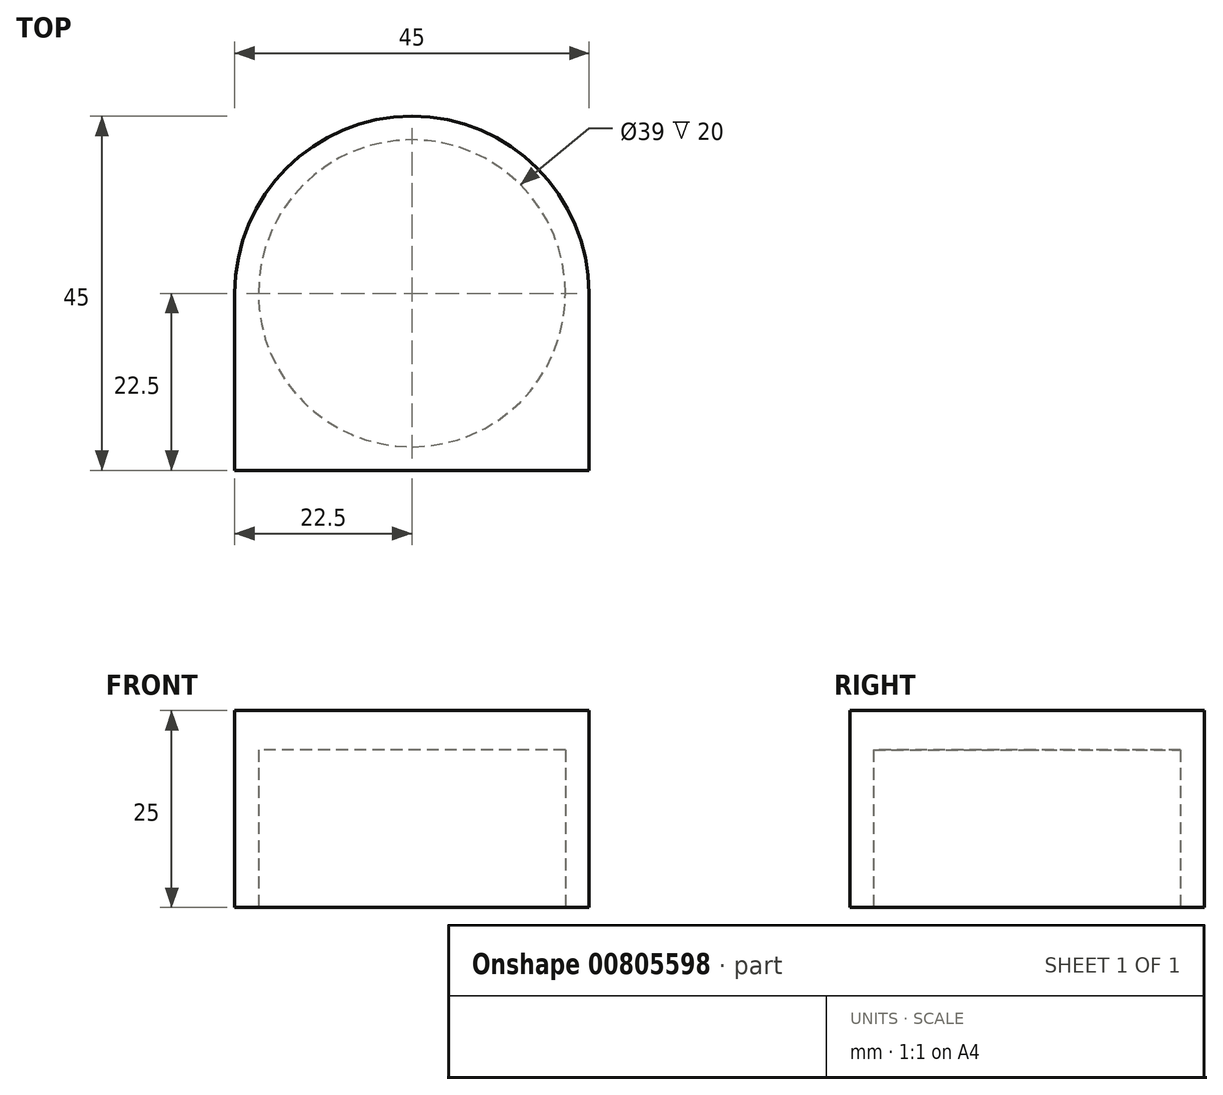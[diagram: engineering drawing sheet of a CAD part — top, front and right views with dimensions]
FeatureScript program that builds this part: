
annotation { "Feature Type Name" : "Feature", "Feature Type Description" : "" }
export const myFeature = defineFeature(function(context is Context, id is Id, definition is map)
    precondition{}
    {
        {
            var Q0;
            Q0=qCreatedBy(makeId("Top.planeOp"),FACE);
            var sketch = newSketch(context, id + "F0", { "sketchPlane" : qUnion([Q0])});
            skCircle(sketch, "E0", {"center": v(0, 0) * mm, "radius": 22.5 * mm});
            skSolve(sketch);
        }
        {
            var Q0;
            Q0 = qSketchRegion(id + "F0", true);
            extrude(context, id + "F1", {"entities" : qUnion([Q0]), "depth" : 25 * mm, "offsetDistance" : 25 * mm});
        }
        {
            var Q0;
            Q0=qCreatedBy(makeId("Top.planeOp"),FACE);
            var sketch = newSketch(context, id + "F2", { "sketchPlane" : qUnion([Q0])});
            skCircle(sketch, "E1", {"center": v(0, 0) * mm, "radius": 19.5 * mm});
            skSolve(sketch);
        }
        {
            var Q0;
            Q0 = qSketchRegion(id + "F2", true);
            extrude(context, id + "F3", {"entities" : qUnion([Q0]), "operationType" : NewBodyOperationType.REMOVE, "depth" : 20 * mm, "offsetDistance" : 25 * mm});
        }
        {
            var Q0;
            Q0=makeQuery(id+"F1.opExtrude","CAP_FACE",FACE,{"disambiguationData":[OSD([sQuery(id+"F0.wireOp",EDGE,"E0")])],"isStart":true});
            var sketch = newSketch(context, id + "F4", { "sketchPlane" : qUnion([Q0])});
            skLineSegment(sketch, "E2.bottom", {"start": v(22.5, -22.5) * mm, "end": v(-22.5, -22.5) * mm});
            skLineSegment(sketch, "E2.top", {"start": v(22.5, 22.5) * mm, "end": v(-22.5, 22.5) * mm});
            skLineSegment(sketch, "E2.left", {"start": v(22.5, -22.5) * mm, "end": v(22.5, 22.5) * mm});
            skLineSegment(sketch, "E2.right", {"start": v(-22.5, -22.5) * mm, "end": v(-22.5, 22.5) * mm});
            skPoint(sketch, "E2.middle", {"position": v(0, 0) * mm});
            skSolve(sketch);
        }
        {
            var Q0;
            {var subQ0=sQuery(id+"F4.wireOp",EDGE,"E2.right");var subQ1=sQuery(id+"F4.wireOp",EDGE,"E2.top");var subQ2=makeQuery(id+"F4.imprint","INTERSECT",VERTEX,{"derivedFrom":[subQ1,subQ0]});Q0=makeQuery(id+"F4.imprint","IMPRINT",FACE,{"disambiguationData":[TD([[makeQuery(id+"F4.imprint","IMPRINT",EDGE,{"disambiguationData":[TD([[subQ2,1.0]])],"derivedFrom":subQ1}),1.0]])]});}
            var Q1;
            {var subQ0=sQuery(id+"F4.wireOp",EDGE,"E2.left");var subQ1=sQuery(id+"F4.wireOp",EDGE,"E2.top");var subQ2=makeQuery(id+"F4.imprint","INTERSECT",VERTEX,{"derivedFrom":[subQ1,subQ0]});Q1=makeQuery(id+"F4.imprint","IMPRINT",FACE,{"disambiguationData":[TD([[makeQuery(id+"F4.imprint","IMPRINT",EDGE,{"disambiguationData":[TD([[subQ2,-1.0]])],"derivedFrom":subQ1}),1.0]])]});}
            extrude(context, id + "F5", {"entities" : qUnion([Q0, Q1]), "operationType" : NewBodyOperationType.ADD, "oppositeDirection" : true, "depth" : 25 * mm, "offsetDistance" : 25 * mm});
        }
    });
